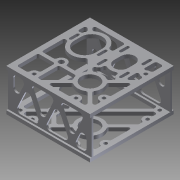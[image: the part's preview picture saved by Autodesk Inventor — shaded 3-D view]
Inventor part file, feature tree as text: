
AUTODESK INVENTOR PART (.ipt)
format: ipt  version: 2012 (Build 160160000, 160)  size: 871,936 bytes
history: native  units: in
note: dims shown in document units (in); Inventor stores cm internally (conversion verified against a paired STEP export)
features: extrude x7, sketch x5, fillet x3, projected_geometry x1
ambient origin geometry x8: Origin, YZ Plane, XZ Plane, XY Plane, X Axis, Y Axis, Z Axis, Center Point
bodies: Solid1 (feature_tree)
feature tree (16):
  extrude  "Extrusion1"  Depth=0.1875in
  sketch  "Sketch2"  dims[d4=0.25in d5=0.25in d6=6.0in d7=0.0in]
  extrude  "Extrusion2"  Depth=6.0in TaperAngle=0.0deg
  extrude  "Extrusion3"  Depth=1.25in
  extrude  "Extrusion4"  Depth=1.625in
  fillet  "Fillet2"  Radius=0.375in
  sketch  "Sketch6"  dims[d20=0.25in d21=0.125in d22=0.25in d24=0.25in d25=0.125in d27=0.125in d32=0.25in d33=0.0in d35=0.375in d36=0.375in d37=0.375in d38=0.375in d39=0.1719in d40=0.3438in d41=0.3438in d42=0.3438in d43=0.3438in d44=0.125in d46=0.125in d49=0.125in d50=0.125in d51=0.125in d52=0.125in d53=0.125in d54=0.125in d55=0.125in d56=0.125in d57=0.25in d58=0.0in d59=0.1719in d60=0.3438in d61=0.3438in d62=0.3438in d63=0.3438in d64=0.125in d65=0.125in d66=0.125in d67=0.125in d68=0.125in d69=0.125in d70=0.125in d71=0.125in d72=0.125in d73=0.125in d74=0.375in d76=0.375in d77=0.375in d78=0.375in d79=0.25in d80=0.0in d81=0.25in d88=0.125in d89=1.25in d90=1.5in d91=0.75in d92=0.5in d94=0.2in d96=0.9in d97=1.0in d98=0.5in d99=0.5in d101=2.0in d102=0.2in d103=0.8in d104=0.8in d105=0.7874in d107=1.6in d108=0.7874in d110=1.6in d114=1.0in d115=1.0in d116=1.625in d117=1.0in d119=0.2in d122=4.5in d123=1.3125in d124=0.366in d126=2.3in d127=0.25in d128=0.0in d129=0.375in d131=4.5in d132=0.125in d153=0.25in d154=0.125in d156=0.375in d157=0.375in d160=0.25in d161=0.125in d162=0.25in d163=0.125in d165=0.875in d166=0.125in d168=0.375in d169=0.25in d170=0.125in d171=1.0in d172=0.25in d177=0.125in d178=0.6in d179=0.25in d180=0.0in d181=0.125in d183=0.25in d185=0.25in d186=0.125in d188=1.5625in d190=1.3125in d191=0.366in d193=0.25in d194=0.125in d197=1.0in d198=1.176in d199=0.1in d200=0.0in d201=0.125in d203=0.25in d204=0.25in d205=0.125in d207=2.1875in d208=2.0312in d211=0.125in d212=0.3in d213=0.5in d214=0.25in d215=0.3125in d220=0.5in d221=1.5in d222=0.25in d224=0.1875in d225=2.3in d226=0.35in d227=0.25in d228=1.5in d229=1.5in d230=0.5821in d231=0.25in d232=1.5in d233=0.125in d234=0.25in d235=2.0in d236=0.25in d237=1.5in d238=0.3125in d239=0.7874in d241=3.0in d242=0.3937in d244=1.0in d246=1.5in d247=0.7874in d249=3.0in d250=0.3937in d252=1.0in d254=0.5in d255=0.25in d256=0.3125in d257=0.25in d258=0.5in d259=0.3125in d260=0.25in d262=0.75in d264=6.0in d267=0.25in d269=3.0in d270=6.0in d272=0.25in d273=0.125in d274=0.125in]
  fillet  "Fillet3"  Radius=0.875in
  extrude  "Extrusion5"  Depth=0.125in
  extrude  "Extrusion6"  Depth=0.25in
  fillet  "Fillet4"  Radius=0.25in
  extrude  "Extrusion7"  Depth=0.125in
  sketch  "Sketch1"  dims[d1=3.0in d2=0.1875in d3=0.25in]
  sketch  "Sketch4"  dims[d11=2.0312in d13=1.25in]
  sketch  "Sketch5"  dims[d15=2.625in d16=1.625in d18=0.375in d19=0.875in]
  projected_geometry  "Projected Loop1"
